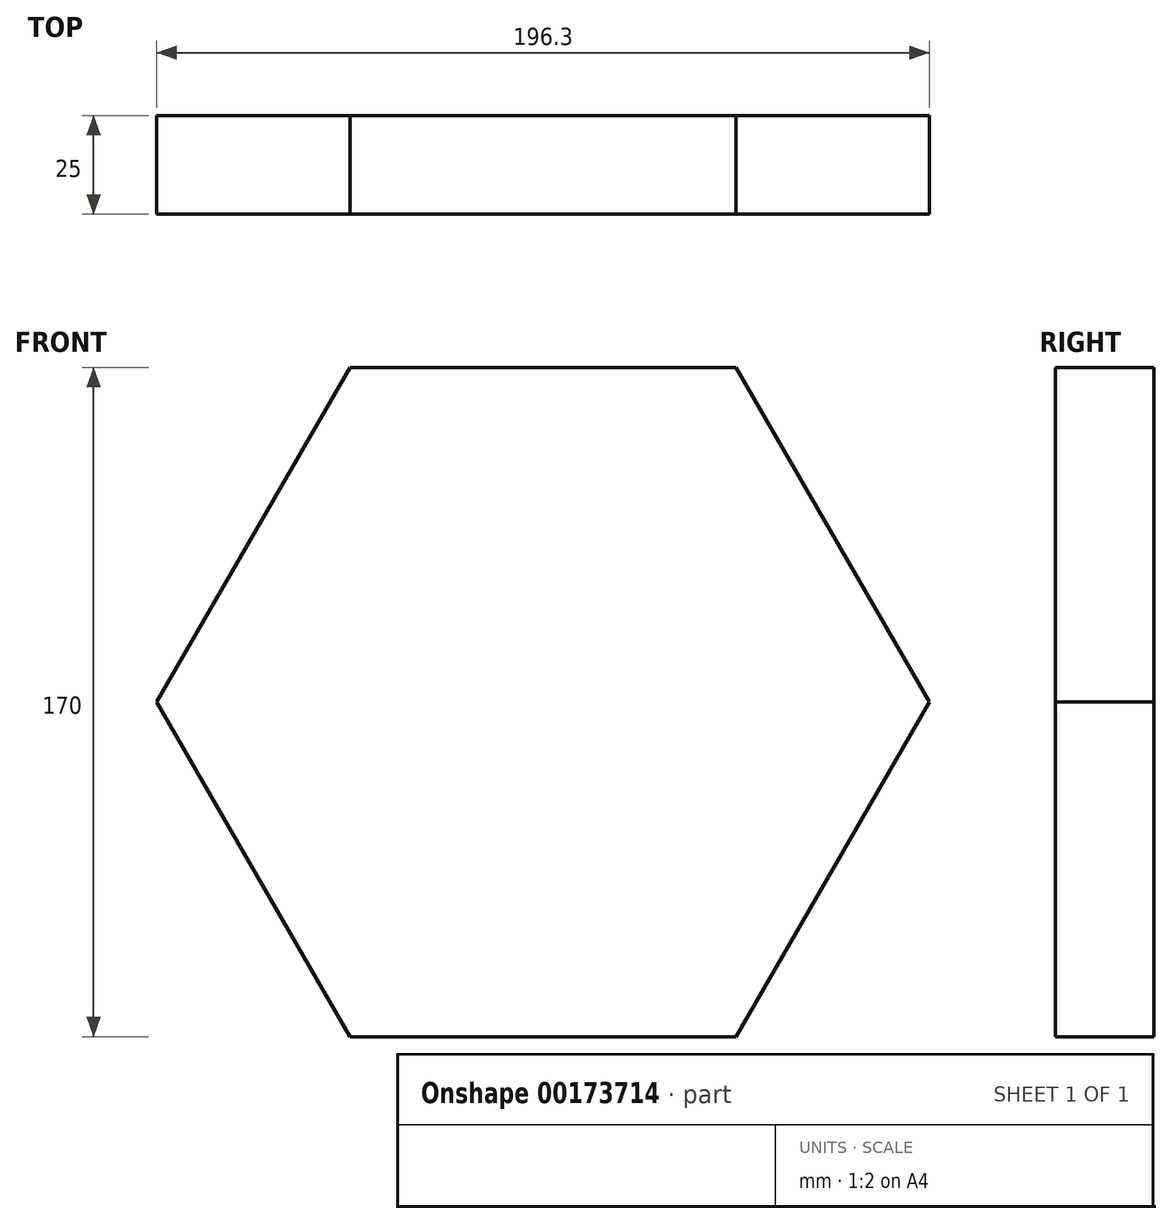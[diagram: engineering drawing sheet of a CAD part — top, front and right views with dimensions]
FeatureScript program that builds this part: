
annotation { "Feature Type Name" : "Feature", "Feature Type Description" : "" }
export const myFeature = defineFeature(function(context is Context, id is Id, definition is map)
    precondition{}
    {
        {
            var Q0;
            Q0=qCreatedBy(makeId("Front.planeOp"),FACE);
            var sketch = newSketch(context, id + "F0", { "sketchPlane" : qUnion([Q0])});
            skCircle(sketch, "E0.cCircle", {"center": v(0, 0) * mm, "radius": 85 * mm, "construction": true});
            skLineSegment(sketch, "E0.0", {"start": v(49.07, 85) * mm, "end": v(98.15, 0) * mm});
            skLineSegment(sketch, "E0.1", {"start": v(98.15, 0) * mm, "end": v(49.07, -85) * mm});
            skLineSegment(sketch, "E0.2", {"start": v(49.07, -85) * mm, "end": v(-49.07, -85) * mm});
            skLineSegment(sketch, "E0.3", {"start": v(-49.07, -85) * mm, "end": v(-98.15, 0) * mm});
            skLineSegment(sketch, "E0.4", {"start": v(-98.15, 0) * mm, "end": v(-49.07, 85) * mm});
            skLineSegment(sketch, "E0.5", {"start": v(-49.07, 85) * mm, "end": v(49.07, 85) * mm});
            skPoint(sketch, "E0.0.midPoint", {"position": v(73.61, 42.5) * mm});
            skSolve(sketch);
        }
        {
            var Q0;
            Q0 = qSketchRegion(id + "F0", true);
            extrude(context, id + "F1", {"entities" : qUnion([Q0]), "depth" : 25 * mm});
        }
    });
